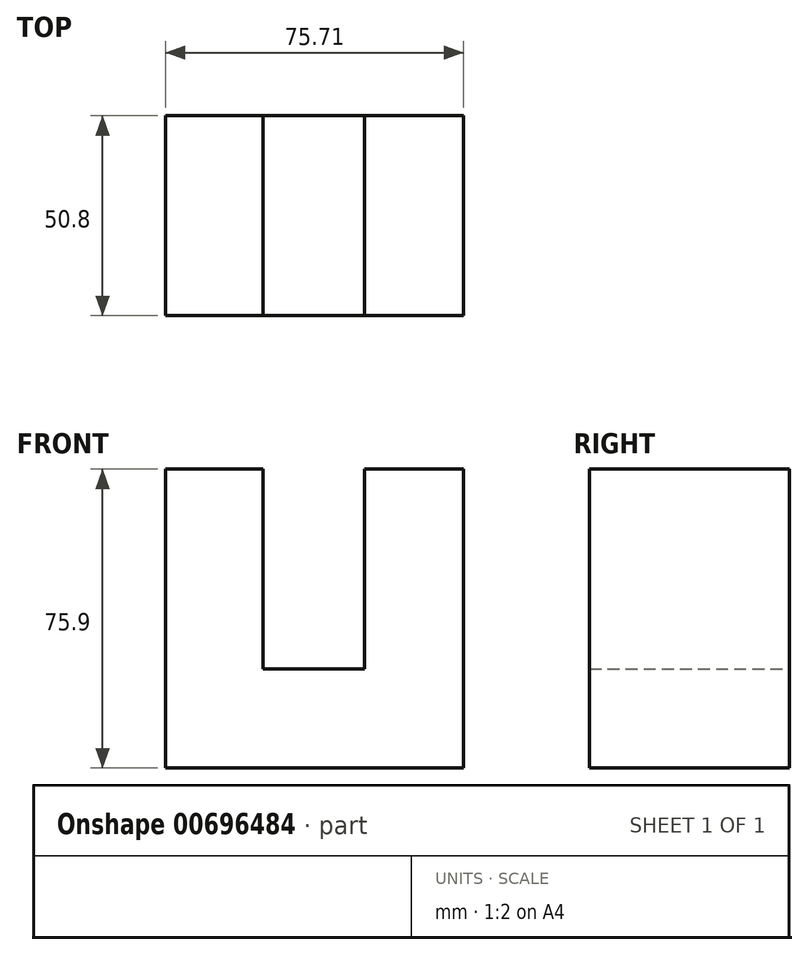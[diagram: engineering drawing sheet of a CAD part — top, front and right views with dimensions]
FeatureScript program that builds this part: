
annotation { "Feature Type Name" : "Feature", "Feature Type Description" : "" }
export const myFeature = defineFeature(function(context is Context, id is Id, definition is map)
    precondition{}
    {
        {
            var Q0;
            Q0=qCreatedBy(makeId("Front.planeOp"),FACE);
            var sketch = newSketch(context, id + "F0", { "sketchPlane" : qUnion([Q0])});
            skLineSegment(sketch, "E0", {"start": v(0, 0) * mm, "end": v(0, 75.9) * mm});
            skLineSegment(sketch, "E1", {"start": v(0, 0) * mm, "end": v(75.71, 0) * mm});
            skLineSegment(sketch, "E2", {"start": v(75.71, 0) * mm, "end": v(75.71, 75.9) * mm});
            skLineSegment(sketch, "E3", {"start": v(75.71, 75.9) * mm, "end": v(50.5, 75.9) * mm});
            skLineSegment(sketch, "E4", {"start": v(0, 75.9) * mm, "end": v(24.73, 75.9) * mm});
            skLineSegment(sketch, "E5", {"start": v(24.73, 75.9) * mm, "end": v(24.73, 25.11) * mm});
            skLineSegment(sketch, "E6", {"start": v(50.5, 75.9) * mm, "end": v(50.5, 25.11) * mm});
            skLineSegment(sketch, "E7", {"start": v(24.73, 25.11) * mm, "end": v(50.5, 25.11) * mm});
            skSolve(sketch);
        }
        {
            var Q0;
            Q0=makeQuery(id+"F0.imprint","IMPRINT",FACE,{"disambiguationData":[TD([[makeQuery(id+"F0.imprint","IMPRINT",EDGE,{"derivedFrom":sQuery(id+"F0.wireOp",EDGE,"E0")}),-1.0]])]});
            extrude(context, id + "F1", {"entities" : qUnion([Q0]), "depth" : 50.8 * mm, "offsetDistance" : 25.4 * mm});
        }
    });
